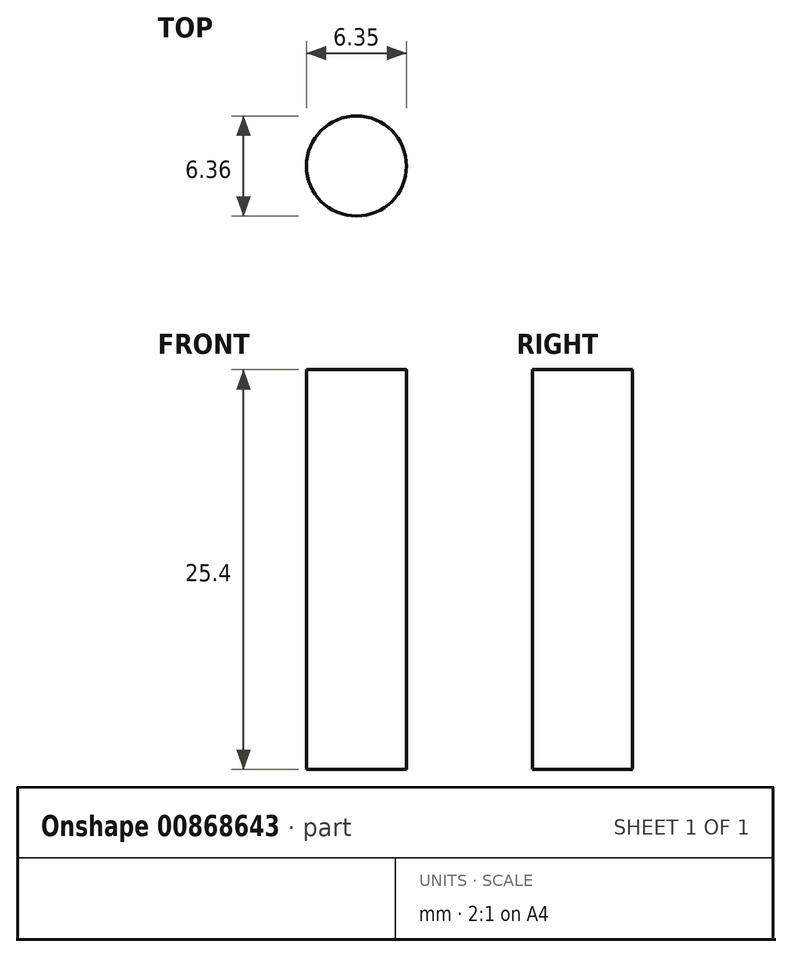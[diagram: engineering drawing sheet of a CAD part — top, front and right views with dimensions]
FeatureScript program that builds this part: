
annotation { "Feature Type Name" : "Feature", "Feature Type Description" : "" }
export const myFeature = defineFeature(function(context is Context, id is Id, definition is map)
    precondition{}
    {
        {
            var Q0;
            Q0=qCreatedBy(makeId("Top.planeOp"),FACE);
            var sketch = newSketch(context, id + "F0", { "sketchPlane" : qUnion([Q0])});
            skCircle(sketch, "E0", {"center": v(0.99, 0) * mm, "radius": 3.17 * mm});
            skSolve(sketch);
        }
        {
            var Q0;
            Q0=makeQuery(id+"F0.imprint","IMPRINT",FACE,{"disambiguationData":[TD([[makeQuery(id+"F0.imprint","IMPRINT",EDGE,{"derivedFrom":sQuery(id+"F0.wireOp",EDGE,"E0")}),1.0]])]});
            extrude(context, id + "F1", {"entities" : qUnion([Q0]), "depth" : 25.4 * mm, "offsetDistance" : 25.4 * mm});
        }
    });
